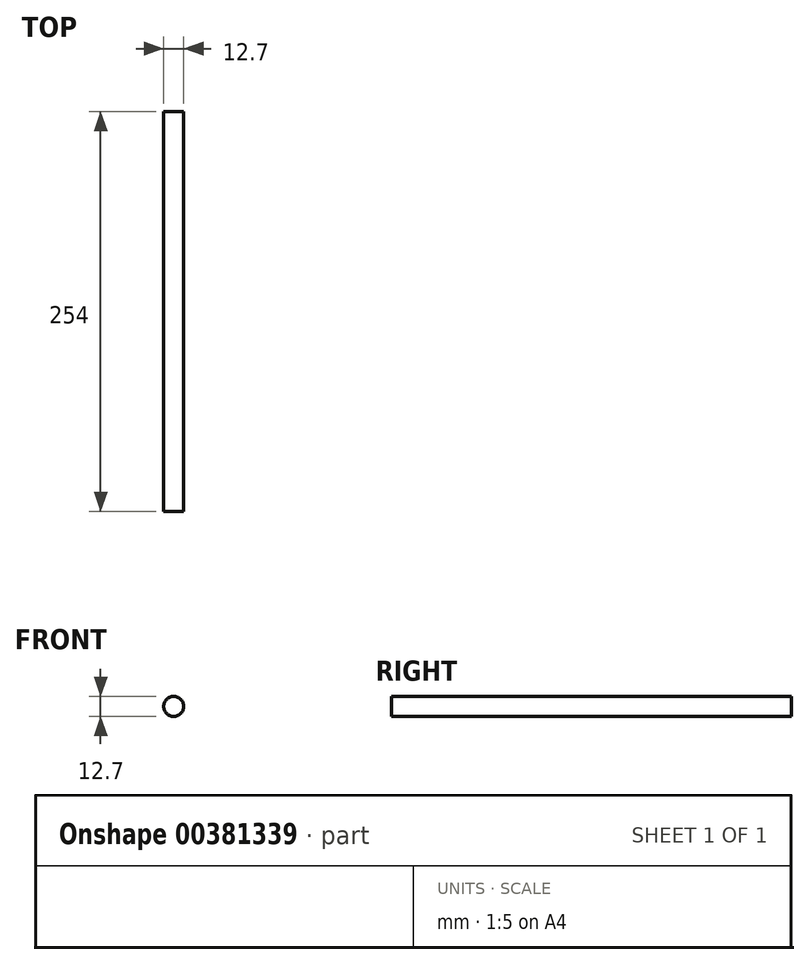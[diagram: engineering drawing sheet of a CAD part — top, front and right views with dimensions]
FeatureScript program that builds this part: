
annotation { "Feature Type Name" : "Feature", "Feature Type Description" : "" }
export const myFeature = defineFeature(function(context is Context, id is Id, definition is map)
    precondition{}
    {
        {
            var Q0;
            Q0=qCreatedBy(makeId("Front.planeOp"),FACE);
            var sketch = newSketch(context, id + "F0", { "sketchPlane" : qUnion([Q0])});
            skCircle(sketch, "E0", {"center": v(0, 0) * mm, "radius": 6.35 * mm});
            skSolve(sketch);
        }
        {
            var Q0;
            Q0=qSketchRegion(id+"F0",true);
            extrude(context, id + "F1", {"entities" : qUnion([Q0]), "endBound" : BoundingType.SYMMETRIC, "depth" : 254 * mm});
        }
    });
